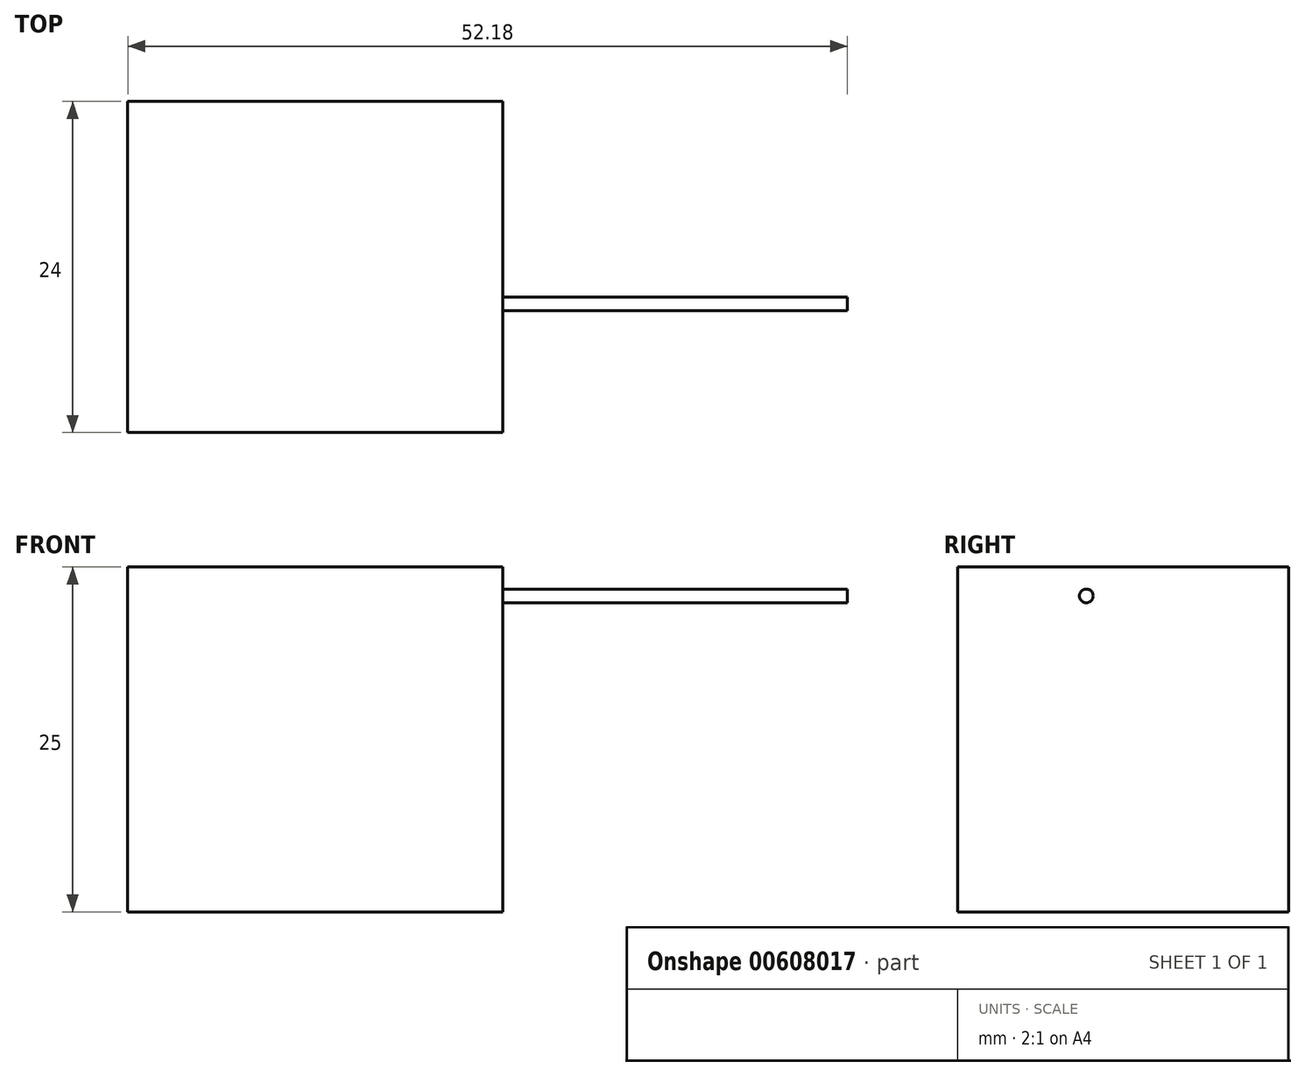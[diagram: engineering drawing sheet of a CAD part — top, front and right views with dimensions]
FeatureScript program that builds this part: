
annotation { "Feature Type Name" : "Feature", "Feature Type Description" : "" }
export const myFeature = defineFeature(function(context is Context, id is Id, definition is map)
    precondition{}
    {
        {
            var Q0;
            Q0=qCreatedBy(makeId("Top.planeOp"),FACE);
            var sketch = newSketch(context, id + "F0", { "sketchPlane" : qUnion([Q0])});
            skLineSegment(sketch, "E0.bottom", {"start": v(13.6, -9.33) * mm, "end": v(-13.6, -9.33) * mm});
            skLineSegment(sketch, "E0.top", {"start": v(13.6, 14.67) * mm, "end": v(-13.6, 14.67) * mm});
            skLineSegment(sketch, "E0.left", {"start": v(13.6, -9.33) * mm, "end": v(13.6, 14.67) * mm});
            skLineSegment(sketch, "E0.right", {"start": v(-13.6, -9.33) * mm, "end": v(-13.6, 14.67) * mm});
            skPoint(sketch, "E0.middle", {"position": v(0, 2.67) * mm});
            skSolve(sketch);
        }
        {
            var Q0;
            Q0 = qSketchRegion(id + "F0", true);
            extrude(context, id + "F1", {"entities" : qUnion([Q0]), "depth" : 25 * mm, "offsetDistance" : 25 * mm});
        }
        {
            var Q0;
            Q0=makeQuery(id+"F1.opExtrude","SWEPT_FACE",FACE,{"disambiguationData":[OSD([sQuery(id+"F0.wireOp",EDGE,"E0.left")])]});
            var sketch = newSketch(context, id + "F2", { "sketchPlane" : qUnion([Q0])});
            skCircle(sketch, "E1", {"center": v(0, 22.9) * mm, "radius": 0.5 * mm});
            skSolve(sketch);
        }
        {
            var Q0;
            Q0 = qSketchRegion(id + "F2", true);
            extrude(context, id + "F3", {"entities" : qUnion([Q0]), "operationType" : NewBodyOperationType.ADD, "depth" : 25 * mm, "offsetDistance" : 25 * mm});
        }
    });
